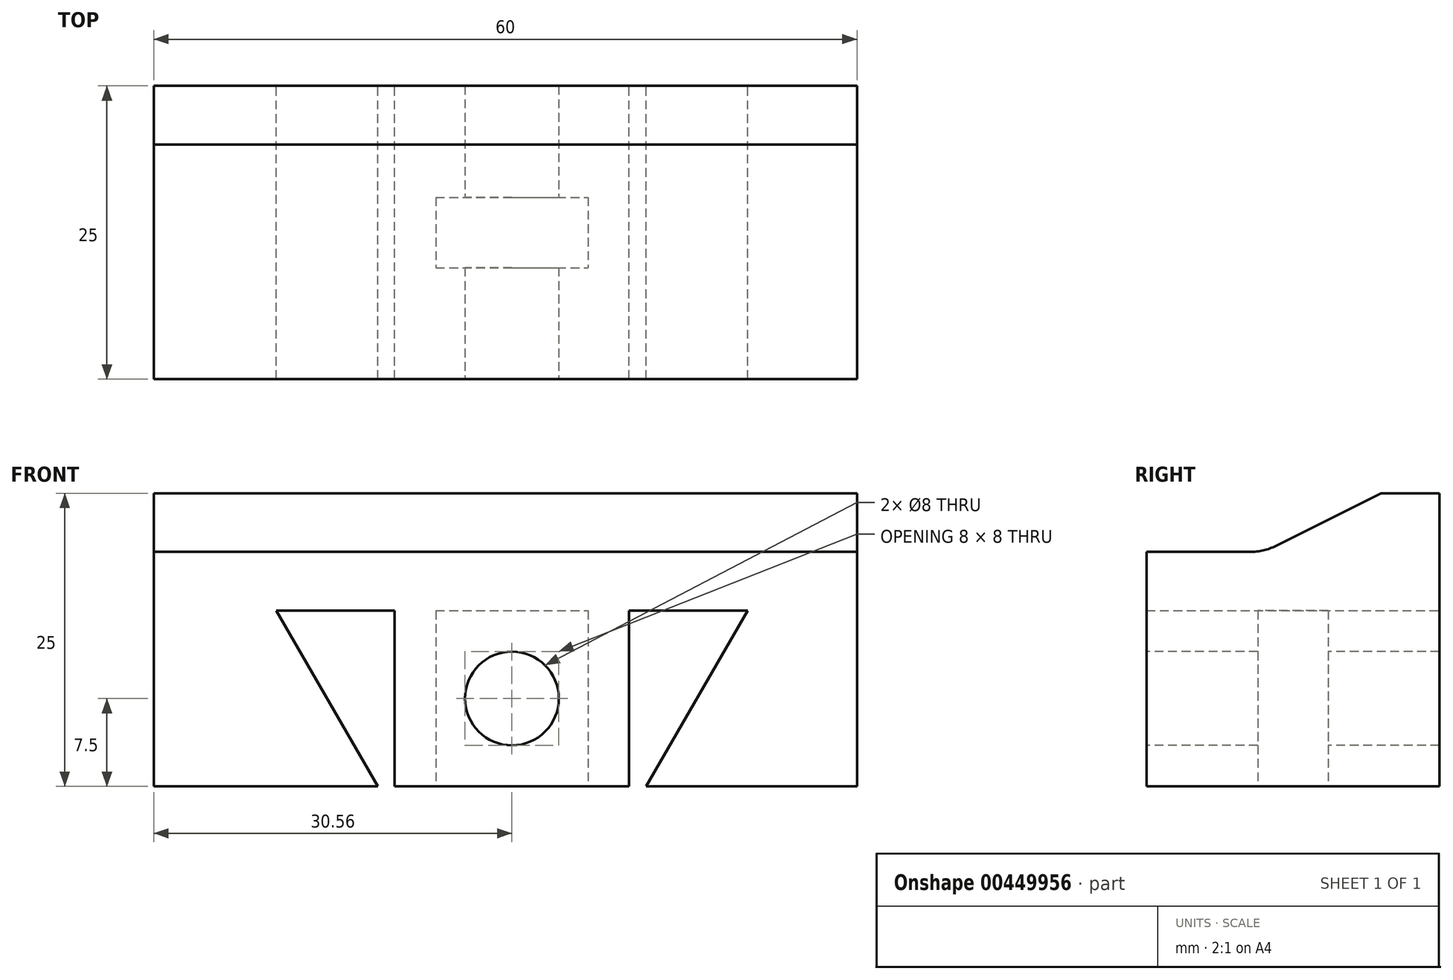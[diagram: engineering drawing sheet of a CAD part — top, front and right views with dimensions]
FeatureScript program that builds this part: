
annotation { "Feature Type Name" : "Feature", "Feature Type Description" : "" }
export const myFeature = defineFeature(function(context is Context, id is Id, definition is map)
    precondition{}
    {
        {
            var Q0;
            Q0=qCreatedBy(makeId("Front.planeOp"),FACE);
            var sketch = newSketch(context, id + "F0", { "sketchPlane" : qUnion([Q0])});
            skLineSegment(sketch, "E0.bottom", {"start": v(-30.56, 17.5) * mm, "end": v(29.44, 17.5) * mm});
            skLineSegment(sketch, "E0.top", {"start": v(-30.56, -7.5) * mm, "end": v(-11.44, -7.5) * mm});
            skLineSegment(sketch, "E0.left", {"start": v(-30.56, 17.5) * mm, "end": v(-30.56, -7.5) * mm});
            skLineSegment(sketch, "E0.right", {"start": v(29.44, 17.5) * mm, "end": v(29.44, -7.5) * mm});
            skLineSegment(sketch, "E1", {"start": v(-20.1, 7.5) * mm, "end": v(-20.1, -7.5) * mm});
            skLineSegment(sketch, "E2", {"start": v(-20.1, 7.5) * mm, "end": v(-11.44, -7.5) * mm});
            skLineSegment(sketch, "E3", {"start": v(-10, 7.5) * mm, "end": v(-10, -7.5) * mm});
            skLineSegment(sketch, "E4.MirrorCS", {"start": v(20.1, 7.5) * mm, "end": v(11.44, -7.5) * mm});
            skLineSegment(sketch, "E5.MirrorCS", {"start": v(10, 7.5) * mm, "end": v(10, -7.5) * mm});
            skLineSegment(sketch, "E6.trimOffspring", {"start": v(10, 7.5) * mm, "end": v(20.1, 7.5) * mm});
            skLineSegment(sketch, "E7.trimOffspring", {"start": v(-20.1, 7.5) * mm, "end": v(-10, 7.5) * mm});
            skLineSegment(sketch, "E8.trimOffspring", {"start": v(11.44, -7.5) * mm, "end": v(29.44, -7.5) * mm});
            skLineSegment(sketch, "E9.trimOffspring", {"start": v(-10, -7.5) * mm, "end": v(10, -7.5) * mm});
            skSolve(sketch);
        }
        {
            var Q0;
            Q0=makeQuery(id+"F0.imprint","IMPRINT",FACE,{"disambiguationData":[TD([[makeQuery(id+"F0.imprint","IMPRINT",EDGE,{"derivedFrom":sQuery(id+"F0.wireOp",EDGE,"E0.bottom")}),-1.0]])]});
            var Q1;
            {var subQ2=sQuery(id+"F0.wireOp",EDGE,"E1");Q1=makeQuery(id+"F0.imprint","IMPRINT",FACE,{"disambiguationData":[TD([[makeQuery(id+"F0.imprint","IMPRINT",EDGE,{"derivedFrom":subQ2}),1.0]])]});}
            extrude(context, id + "F1", {"entities" : qUnion([Q0, Q1]), "depth" : 25 * mm});
        }
        {
            var Q0;
            Q0=makeQuery(id+"F1.opExtrude","SWEPT_FACE",FACE,{"disambiguationData":[OSD([sQuery(id+"F0.wireOp",EDGE,"E0.left")])]});
            var sketch = newSketch(context, id + "F2", { "sketchPlane" : qUnion([Q0])});
            skPoint(sketch, "E10.startSnap0", {"position": v(12.5, 17.5) * mm});
            skLineSegment(sketch, "E11", {"start": v(33.07, 12.5) * mm, "end": v(15, 12.5) * mm});
            skLineSegment(sketch, "E12", {"start": v(5, 23.24) * mm, "end": v(5, 17.5) * mm});
            skLineSegment(sketch, "E13", {"start": v(5, 17.5) * mm, "end": v(15, 12.5) * mm});
            skSolve(sketch);
        }
        {
            var Q0;
            {var subQ0=sQuery(id+"F2.wireOp",EDGE,"E13");Q0=makeQuery(id+"F2.imprint","IMPRINT",FACE,{"disambiguationData":[TD([[makeQuery(id+"F2.imprint","IMPRINT",EDGE,{"derivedFrom":subQ0}),1.0]])]});}
            extrude(context, id + "F3", {"entities" : qUnion([Q0]), "operationType" : NewBodyOperationType.REMOVE, "endBound" : BoundingType.THROUGH_ALL, "oppositeDirection" : true, "depth" : 25 * mm});
        }
        {
            var Q0;
            Q0=makeQuery(id+"F3.boolean.opBoolean","COPY",EDGE,{"derivedFrom":makeQuery(id+"F3.opExtrude","SWEPT_EDGE",EDGE,{"disambiguationData":[OSD([sQuery(id+"F2.wireOp",EDGE,"E11"),sQuery(id+"F2.wireOp",EDGE,"E13")])]})});
            fillet(context, id + "F4", {"entities" : qUnion([Q0]), "radius" : 5 * mm, "tangentPropagation" : true, "allowEdgeOverflow" : false});
        }
        {
            var Q0;
            Q0=makeQuery(id+"F1.opExtrude","SWEPT_FACE",FACE,{"disambiguationData":[OSD([sQuery(id+"F0.wireOp",EDGE,"E9.trimOffspring")])]});
            var sketch = newSketch(context, id + "F5", { "sketchPlane" : qUnion([Q0])});
            skLineSegment(sketch, "E14.bottom", {"start": v(-6.5, 9.5) * mm, "end": v(6.5, 9.5) * mm});
            skLineSegment(sketch, "E14.top", {"start": v(-6.5, 15.5) * mm, "end": v(6.5, 15.5) * mm});
            skLineSegment(sketch, "E14.left", {"start": v(-6.5, 9.5) * mm, "end": v(-6.5, 15.5) * mm});
            skLineSegment(sketch, "E14.right", {"start": v(6.5, 9.5) * mm, "end": v(6.5, 15.5) * mm});
            skSolve(sketch);
        }
        {
            var Q0;
            Q0=makeQuery(id+"F5.imprint","IMPRINT",FACE,{"disambiguationData":[TD([[makeQuery(id+"F5.imprint","IMPRINT",EDGE,{"derivedFrom":sQuery(id+"F5.wireOp",EDGE,"E14.bottom")}),1.0]])]});
            extrude(context, id + "F6", {"entities" : qUnion([Q0]), "operationType" : NewBodyOperationType.REMOVE, "oppositeDirection" : true, "depth" : 15 * mm});
        }
        {
            var Q0;
            Q0=makeQuery(id+"F1.opExtrude","CAP_FACE",FACE,{"disambiguationData":[OSD([sQuery(id+"F0.wireOp",EDGE,"E0.bottom"),sQuery(id+"F0.wireOp",EDGE,"E0.top"),sQuery(id+"F0.wireOp",EDGE,"E0.left"),sQuery(id+"F0.wireOp",EDGE,"E0.right"),sQuery(id+"F0.wireOp",EDGE,"E2"),sQuery(id+"F0.wireOp",EDGE,"E3"),sQuery(id+"F0.wireOp",EDGE,"E4.MirrorCS"),sQuery(id+"F0.wireOp",EDGE,"E5.MirrorCS"),sQuery(id+"F0.wireOp",EDGE,"E6.trimOffspring"),sQuery(id+"F0.wireOp",EDGE,"E7.trimOffspring"),sQuery(id+"F0.wireOp",EDGE,"E8.trimOffspring"),sQuery(id+"F0.wireOp",EDGE,"E9.trimOffspring")])],"isStart":false});
            var sketch = newSketch(context, id + "F7", { "sketchPlane" : qUnion([Q0])});
            skCircle(sketch, "E15", {"center": v(0, 0) * mm, "radius": 4 * mm});
            skSolve(sketch);
        }
        {
            var Q0;
            Q0=makeQuery(id+"F7.imprint","IMPRINT",FACE,{"disambiguationData":[TD([[makeQuery(id+"F7.imprint","IMPRINT",EDGE,{"derivedFrom":sQuery(id+"F7.wireOp",EDGE,"E15")}),1.0]])]});
            extrude(context, id + "F8", {"entities" : qUnion([Q0]), "operationType" : NewBodyOperationType.REMOVE, "endBound" : BoundingType.THROUGH_ALL, "oppositeDirection" : true, "depth" : 25 * mm});
        }
    });
